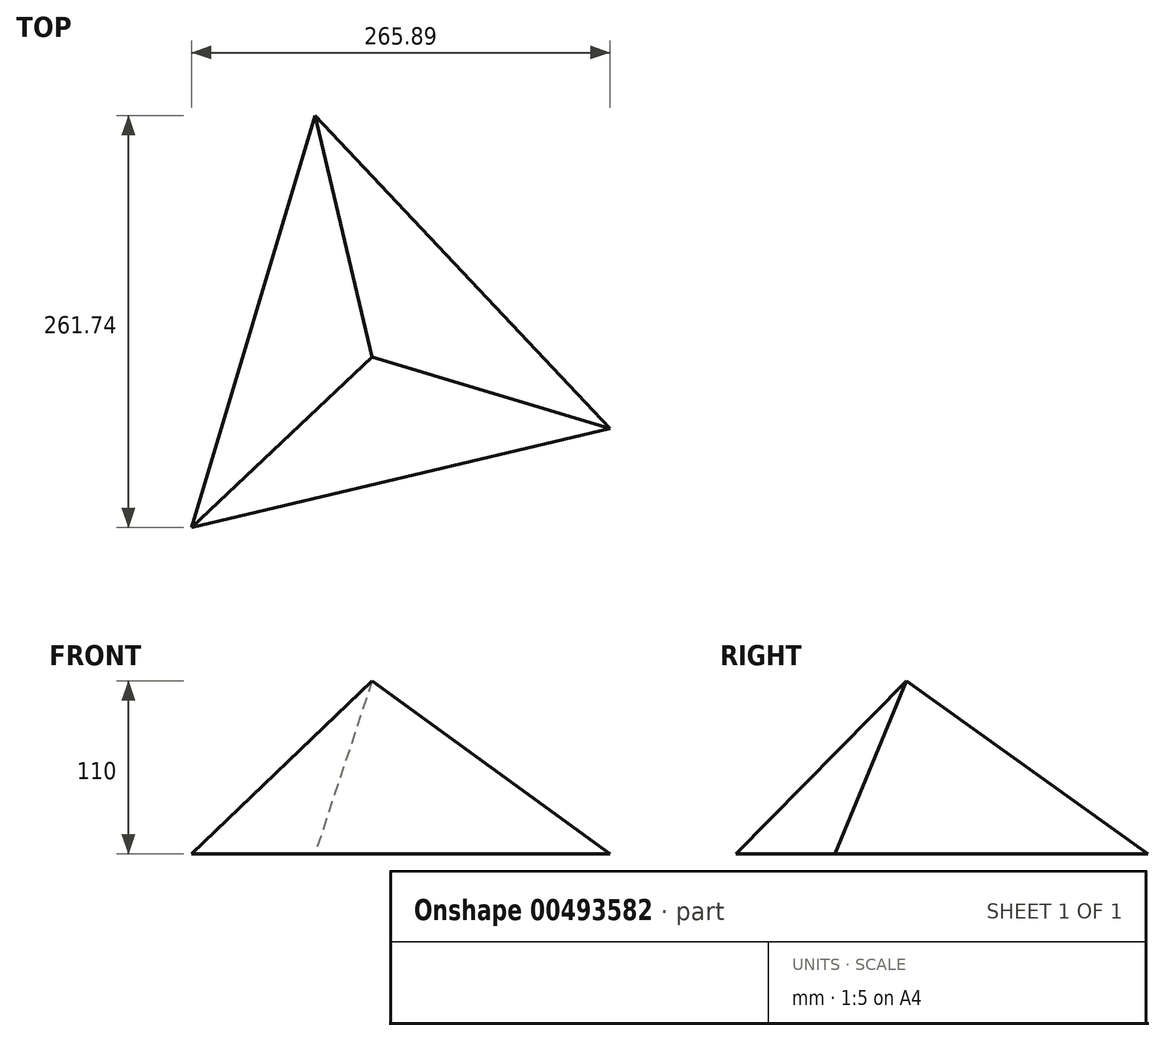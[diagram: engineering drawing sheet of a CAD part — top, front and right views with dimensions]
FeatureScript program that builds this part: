
annotation { "Feature Type Name" : "Feature", "Feature Type Description" : "" }
export const myFeature = defineFeature(function(context is Context, id is Id, definition is map)
    precondition{}
    {
        {
            var Q0;
            Q0=qCreatedBy(makeId("Top.planeOp"),FACE);
            var sketch = newSketch(context, id + "F0", { "sketchPlane" : qUnion([Q0])});
            skCircle(sketch, "E0.cCircle", {"center": v(0, 0) * mm, "radius": 157.76 * mm, "construction": true});
            skLineSegment(sketch, "E0.0", {"start": v(-114.77, -108.23) * mm, "end": v(-36.34, 153.51) * mm});
            skLineSegment(sketch, "E0.1", {"start": v(-36.34, 153.51) * mm, "end": v(151.12, -45.28) * mm});
            skLineSegment(sketch, "E0.2", {"start": v(151.12, -45.28) * mm, "end": v(-114.77, -108.23) * mm});
            skSolve(sketch);
        }
        {
            var Q0;
            Q0=qCreatedBy(makeId("Top.planeOp"),FACE);
            cPlane(context, id + "F1", {"entities" : qUnion([Q0]), "cplaneType" : CPlaneType.OFFSET, "offset" : 110 * mm, "width" : 150 * mm, "height" : 150 * mm});
        }
        {
            var Q0;
            Q0=qCreatedBy(id+"F1.planeOp",FACE);
            var sketch = newSketch(context, id + "F2", { "sketchPlane" : qUnion([Q0])});
            skPoint(sketch, "E1", {"position": v(0, 0) * mm});
            skSolve(sketch);
        }
        {
            var Q0;
            Q0=sQuery(id+"F2.wireOp",VERTEX,"E1");
            var Q1;
            Q1=makeQuery(id+"F0.imprint","IMPRINT",FACE,{"disambiguationData":[TD([[makeQuery(id+"F0.imprint","IMPRINT",EDGE,{"derivedFrom":sQuery(id+"F0.wireOp",EDGE,"E0.0")}),-1.0]])]});
            loft(context, id + "F3", {"sheetProfilesArray" : [{ "sheetProfileEntities" : qUnion([Q0]) }, { "sheetProfileEntities" : qUnion([Q1]) }]});
        }
    });
